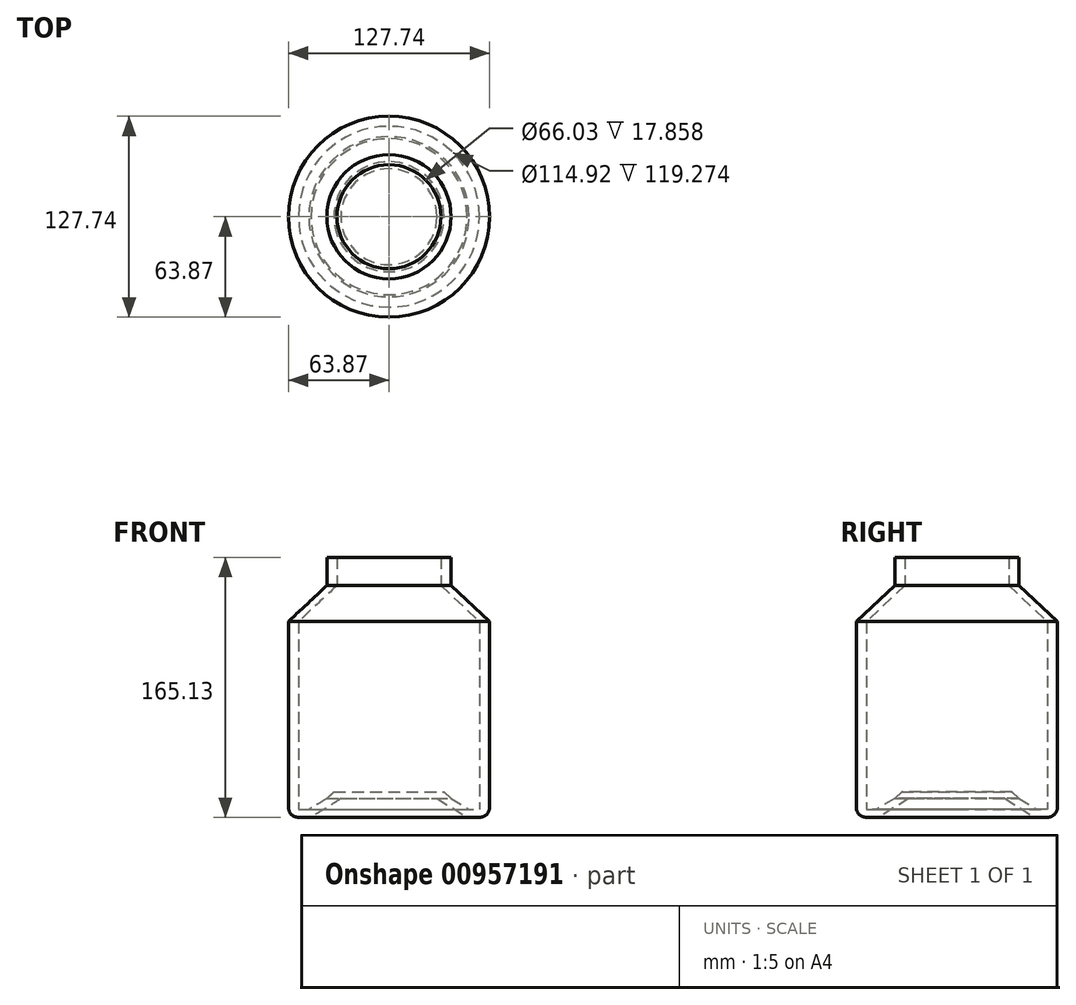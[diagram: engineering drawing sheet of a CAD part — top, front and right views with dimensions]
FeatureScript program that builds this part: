
annotation { "Feature Type Name" : "Feature", "Feature Type Description" : "" }
export const myFeature = defineFeature(function(context is Context, id is Id, definition is map)
    precondition{}
    {
        {
            var Q0;
            Q0=qCreatedBy(makeId("Front.planeOp"),FACE);
            var sketch = newSketch(context, id + "F0", { "sketchPlane" : qUnion([Q0])});
            skLineSegment(sketch, "E0", {"start": v(0, 0) * mm, "end": v(0, 73.13) * mm, "construction": true});
            skLineSegment(sketch, "E1", {"start": v(0, 0) * mm, "end": v(30.46, 0) * mm});
            skLineSegment(sketch, "E2", {"start": v(30.46, 0) * mm, "end": v(49.55, -11.93) * mm});
            skLineSegment(sketch, "E3", {"start": v(49.55, -11.93) * mm, "end": v(57.52, -11.93) * mm});
            skLineSegment(sketch, "E4", {"start": v(63.87, -5.58) * mm, "end": v(63.87, 73.13) * mm});
            skLineSegment(sketch, "E5", {"start": v(63.87, 73.13) * mm, "end": v(63.87, 112.47) * mm});
            skLineSegment(sketch, "E6", {"start": v(63.87, 112.47) * mm, "end": v(39.43, 135.34) * mm});
            skLineSegment(sketch, "E7", {"start": v(39.43, 135.34) * mm, "end": v(39.43, 153.2) * mm});
            skLineSegment(sketch, "E8", {"start": v(39.43, 153.2) * mm, "end": v(33.02, 153.2) * mm});
            skLineSegment(sketch, "E9", {"start": v(33.02, 153.2) * mm, "end": v(33.02, 135.34) * mm});
            skLineSegment(sketch, "E10", {"start": v(33.02, 135.34) * mm, "end": v(57.46, 112.47) * mm});
            skLineSegment(sketch, "E11", {"start": v(57.46, 112.47) * mm, "end": v(57.46, -6.8) * mm});
            skLineSegment(sketch, "E12", {"start": v(57.46, -6.8) * mm, "end": v(50.88, -6.8) * mm});
            skLineSegment(sketch, "E13", {"start": v(50.88, -6.8) * mm, "end": v(39.43, 0) * mm});
            skLineSegment(sketch, "E14", {"start": v(39.43, 0) * mm, "end": v(34.94, 4.2) * mm});
            skLineSegment(sketch, "E15", {"start": v(34.94, 4.2) * mm, "end": v(6.42, 4.2) * mm});
            skLineSegment(sketch, "E16", {"start": v(6.42, 4.2) * mm, "end": v(0, 4.2) * mm});
            skLineSegment(sketch, "E17", {"start": v(0, 4.2) * mm, "end": v(0, 0) * mm});
            skPoint(sketch, "E18.visualSharp", {"position": v(63.87, -11.93) * mm});
            skArc(sketch, "E18.filletArc", {"start": v(57.52, -11.93) * mm, "mid": v(62, -10.07) * mm, "end": v(63.87, -5.58) * mm});
            skSolve(sketch);
        }
        {
            var Q0;
            Q0=makeQuery(id+"F0.imprint","IMPRINT",FACE,{"disambiguationData":[TD([[makeQuery(id+"F0.imprint","IMPRINT",EDGE,{"derivedFrom":sQuery(id+"F0.wireOp",EDGE,"E1")}),1.0]])]});
            var Q1;
            Q1=sQuery(id+"F0.wireOp",EDGE,"E0");
            revolve(context, id + "F1", {"surfaceOperationType" : NewSurfaceOperationType.NEW, "entities" : qUnion([Q0]), "axis" : qUnion([Q1]), "revolveType" : RevolveType.FULL});
        }
    });
